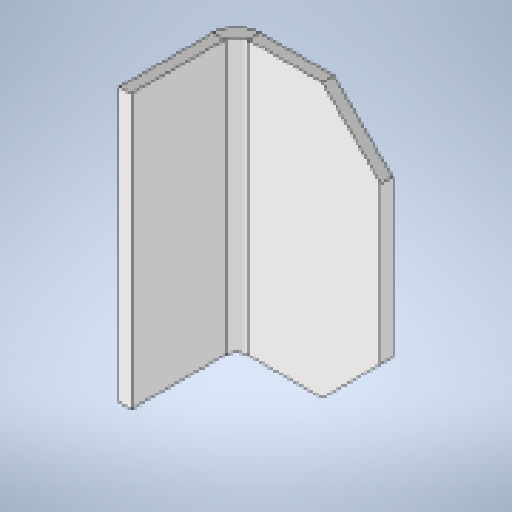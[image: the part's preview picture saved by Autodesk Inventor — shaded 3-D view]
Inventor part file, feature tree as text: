
AUTODESK INVENTOR PART (.ipt)
format: ipt  version: 2025.1 (Build 291241020, 241B)  size: 176,640 bytes
history: native  units: mm
features: sheet_metal_op x4, other x3, sketch x2
ambient origin geometry x8: Origin, YZ Plane, XZ Plane, XY Plane, X Axis, Y Axis, Z Axis, Center Point
bodies: Solid1 (feature_tree)
feature tree (9):
  sheet_metal_op  "Face1"
  sheet_metal_op  "Flange1"
  sketch  "Sketch1"  dims[d1=140.0mm]
  other  "Plate1"
  sketch  "Sketch3"  dims[d2=6.0mm d15=30.0mm d17=6.0mm d18=3.0mm d19=12.0mm d20=6.0mm d21=60.0mm d22=90.0deg d23=6.0mm d24=24.0mm d25=6.0mm d26=6.0mm d27=80.0mm d28=45.0deg]
  other  "Plate2"
  sheet_metal_op  "Bend1"
  sheet_metal_op  "Corner1"
  other  "Definition1"
